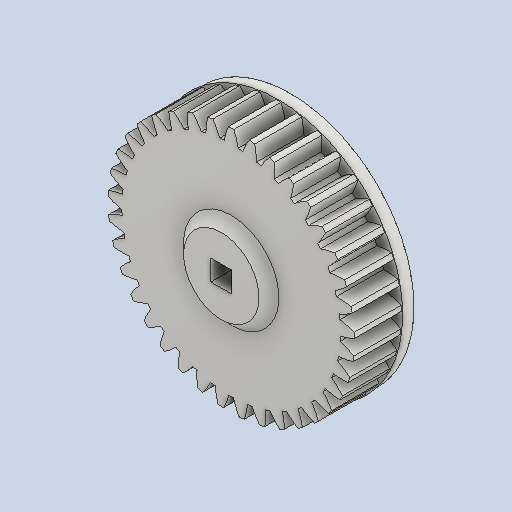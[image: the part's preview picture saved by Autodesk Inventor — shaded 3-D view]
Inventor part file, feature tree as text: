
AUTODESK INVENTOR PART (.ipt)
format: ipt  version: 2022 (Build 260153000, 153)  size: 700,416 bytes
history: native  units: in
note: dims shown in document units (in); Inventor stores cm internally (conversion verified against a paired STEP export)
features: other x12, sketch x5, plane x3
ambient origin geometry x8: Origin, YZ Plane, XZ Plane, XY Plane, X Axis, Y Axis, Z Axis, Center Point
bodies: Solid1 (feature_tree)
feature tree (20):
  other  "Spur Gear2"
  other  "Solid1::Spur Gear2"
  other  "TaggingFeature1"
  sketch  "Sketch1"  dims[d0=0.3937in]
  sketch  "Sketch2"  dims[d9=0.0in d14=0.0in d15=0.9352in d16=0.0in d17=0.0in d18=0.0in d19=0.9352in]
  sketch  "Sketch3"
  sketch  "Sketch4"
  sketch  "Sketch5"
  plane  "XZ Plane_1"
  plane  "Work Plane2"
  plane  "Work Plane3"
  other  "Srf1"
  other  "Srf1::Derived"
  other  "Start plane iMate"
  other  "Distance iMate"
  other  "Position iMate"
  other  "Mesh iMate"
  other  "Axis iMate"
  other  "Mesh iMate2"
  other  "Align iMate"
